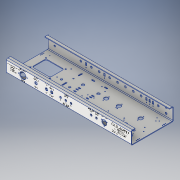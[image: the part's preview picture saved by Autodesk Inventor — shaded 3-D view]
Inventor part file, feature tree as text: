
AUTODESK INVENTOR PART (.ipt)
format: ipt  version: 2018.3 (Build 223285000, 285)  size: 2,185,728 bytes
history: native  units: in
note: dims shown in document units (in); Inventor stores cm internally (conversion verified against a paired STEP export)
features: other x16, sheet_metal_op x13, sketch x10
ambient origin geometry x8: Origin, YZ Plane, XZ Plane, XY Plane, X Axis, Y Axis, Z Axis, Center Point
bodies: Solid1 (feature_tree)
feature tree (39):
  sheet_metal_op  "Face1"
  sketch  "Sketch2"  dims[d0=23.75in]
  sheet_metal_op  "Flange1"
  sheet_metal_op  "Flange2"
  sheet_metal_op  "Flange3"
  sheet_metal_op  "Flange4"
  other  "Decal1"
  other  "Decal2"
  sketch  "Sketch11"  dims[d13=0.125in d14=0.125in d17=0.125in d18=0.0625in d19=0.25in d20=0.125in d21=0.75in d22=90.0deg d23=0.125in d24=0.5in d25=0.125in d26=0.125in d27=0.125in d28=0.0in d29=0.125in d30=0.0625in d31=0.25in d32=0.125in d33=2.5in d34=90.0deg d35=0.125in d36=0.5in d37=0.125in d38=0.125in d39=0.125in d40=0.0625in d41=0.25in d42=0.125in d43=0.75in d44=90.0deg d45=0.125in d46=0.5in d47=0.125in d48=0.125in d49=0.125in d50=0.0in d439=0.125in d440=0.0in]
  other  "Plate1"
  sketch  "Sketch3"  dims[d1=8.05in]
  other  "Plate2"
  sheet_metal_op  "Bend1"
  sheet_metal_op  "Corner1"
  sketch  "Sketch4"  dims[d2=0.125in]
  other  "Plate3"
  sheet_metal_op  "Bend2"
  sheet_metal_op  "Corner2"
  sketch  "Sketch5"  dims[d5=0.125in]
  sketch  "Sketch6"  dims[d6=0.0625in]
  other  "Plate4"
  sheet_metal_op  "Bend3"
  sheet_metal_op  "Corner3"
  sketch  "Sketch7"  dims[d7=0.25in]
  other  "Plate5"
  sheet_metal_op  "Bend4"
  sheet_metal_op  "Corner4"
  sketch  "Sketch8"  dims[d8=0.125in]
  sketch  "Sketch9"  dims[d9=2.5in d10=90.0deg d11=0.125in]
  sketch  "Sketch10"  dims[d12=0.5in]
  other  "Image6"
  other  "Image7"
  other  "Image8"
  other  "Image20"
  other  "Image21"
  other  "Cut2"
  other  "Cut3"
  other  "Cut4"
  other  "Definition1"
